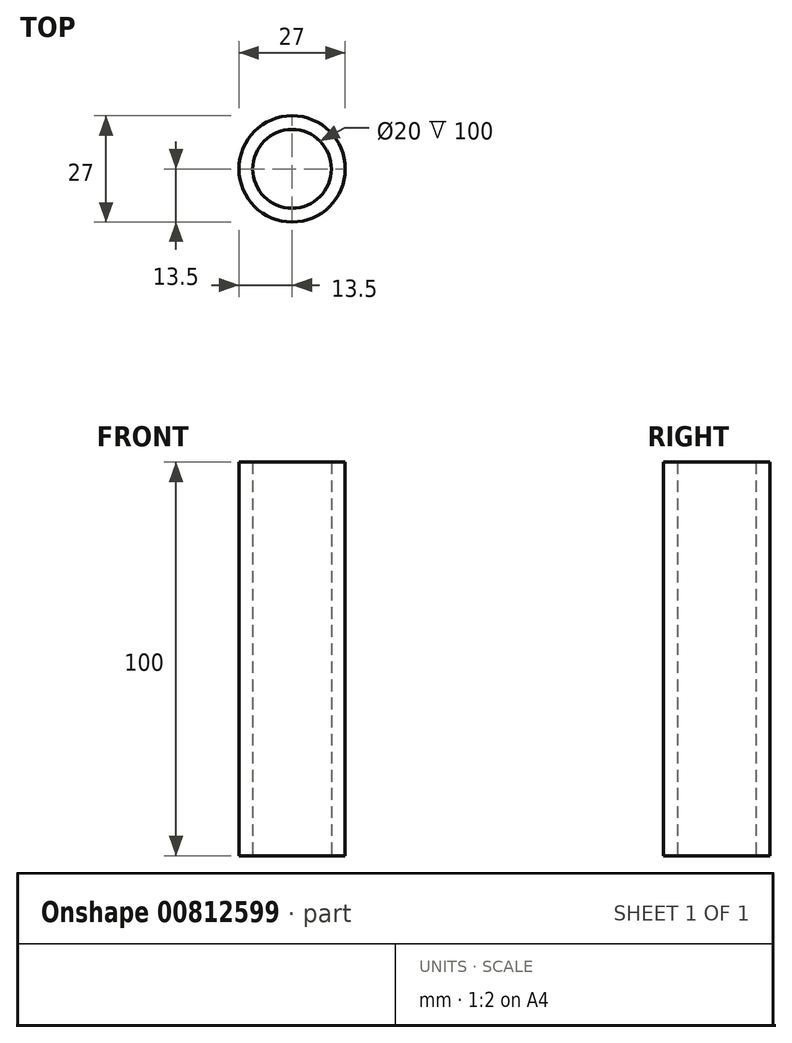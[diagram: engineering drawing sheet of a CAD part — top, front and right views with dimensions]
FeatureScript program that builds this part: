
annotation { "Feature Type Name" : "Feature", "Feature Type Description" : "" }
export const myFeature = defineFeature(function(context is Context, id is Id, definition is map)
    precondition{}
    {
        {
            var Q0;
            Q0=qCreatedBy(makeId("Top.planeOp"),FACE);
            var sketch = newSketch(context, id + "F0", { "sketchPlane" : qUnion([Q0])});
            skCircle(sketch, "E0", {"center": v(0, 0) * mm, "radius": 13.5 * mm});
            skCircle(sketch, "E1", {"center": v(0, 0) * mm, "radius": 10 * mm});
            skSolve(sketch);
        }
        {
            var Q0;
            Q0=makeQuery(id+"F0.imprint","IMPRINT",FACE,{"disambiguationData":[TD([[makeQuery(id+"F0.imprint","IMPRINT",EDGE,{"derivedFrom":sQuery(id+"F0.wireOp",EDGE,"E0")}),1.0]])]});
            extrude(context, id + "F1", {"entities" : qUnion([Q0]), "depth" : 100 * mm, "offsetDistance" : 25 * mm});
        }
    });
